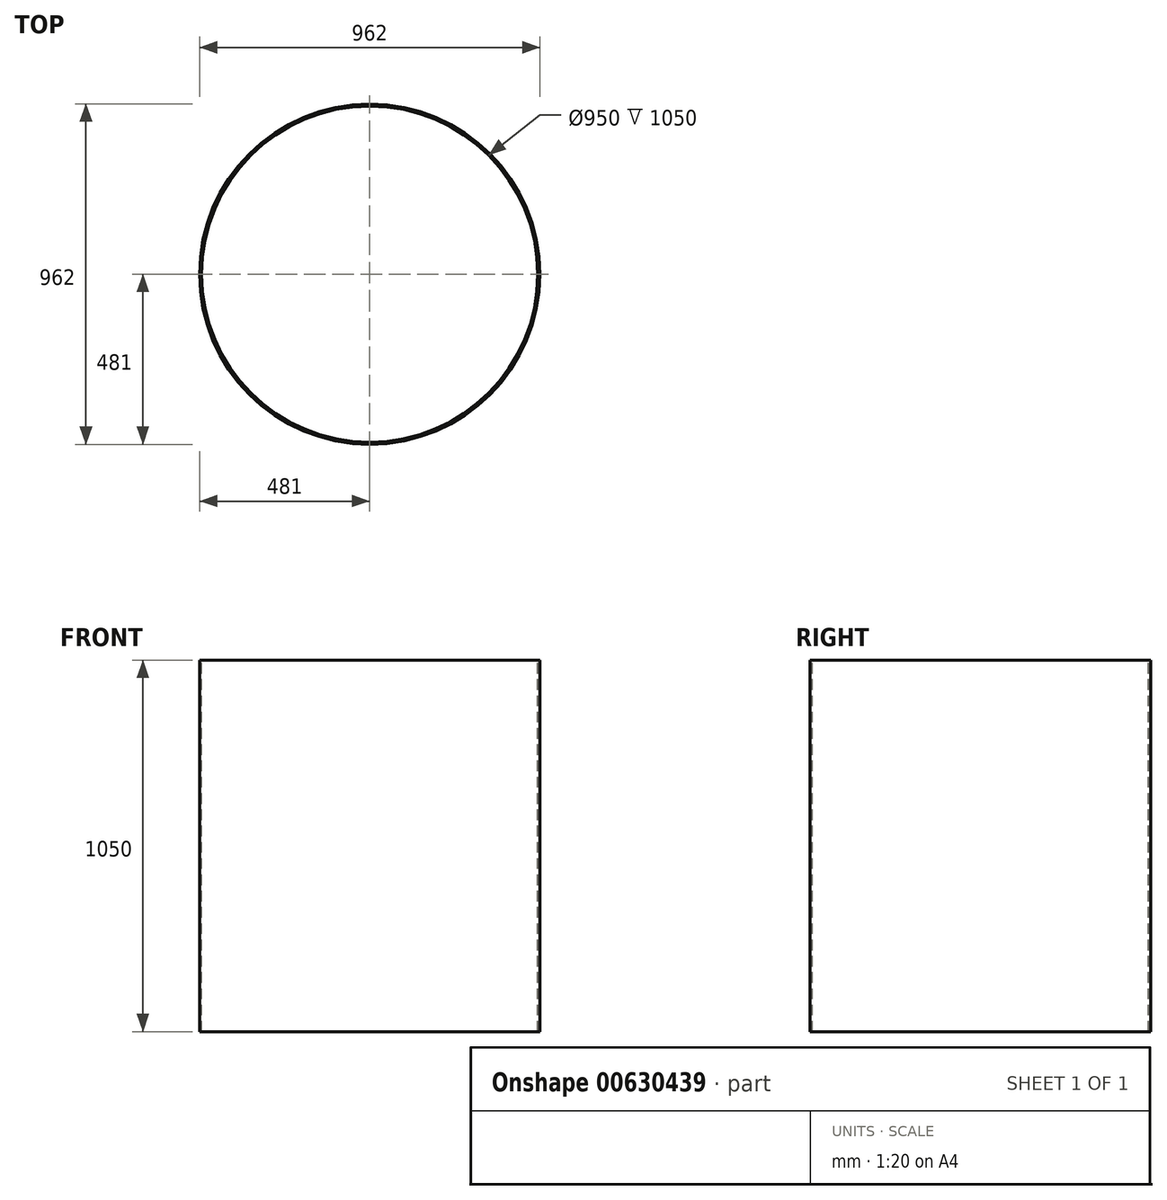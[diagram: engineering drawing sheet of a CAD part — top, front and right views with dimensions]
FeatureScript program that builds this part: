
annotation { "Feature Type Name" : "Feature", "Feature Type Description" : "" }
export const myFeature = defineFeature(function(context is Context, id is Id, definition is map)
    precondition{}
    {
        {
            var Q0;
            Q0=qCreatedBy(makeId("Front.planeOp"),FACE);
            var sketch = newSketch(context, id + "F0", { "sketchPlane" : qUnion([Q0])});
            skLineSegment(sketch, "E0", {"start": v(0, 1259.51) * mm, "end": v(0, -1382.06) * mm, "construction": true});
            skLineSegment(sketch, "E1.bottom", {"start": v(475, 525) * mm, "end": v(481, 525) * mm});
            skLineSegment(sketch, "E1.top", {"start": v(475, -525) * mm, "end": v(481, -525) * mm});
            skLineSegment(sketch, "E1.left", {"start": v(475, 525) * mm, "end": v(475, -525) * mm});
            skLineSegment(sketch, "E1.right", {"start": v(481, 525) * mm, "end": v(481, -525) * mm});
            skSolve(sketch);
        }
        {
            var Q0;
            Q0=makeQuery(id+"F0.imprint","IMPRINT",FACE,{"disambiguationData":[TD([[makeQuery(id+"F0.imprint","IMPRINT",EDGE,{"derivedFrom":sQuery(id+"F0.wireOp",EDGE,"E1.bottom")}),-1.0]])]});
            var Q1;
            Q1=sQuery(id+"F0.wireOp",EDGE,"E0");
            revolve(context, id + "F1", {"entities" : qUnion([Q0]), "axis" : qUnion([Q1]), "revolveType" : RevolveType.FULL});
        }
    });
